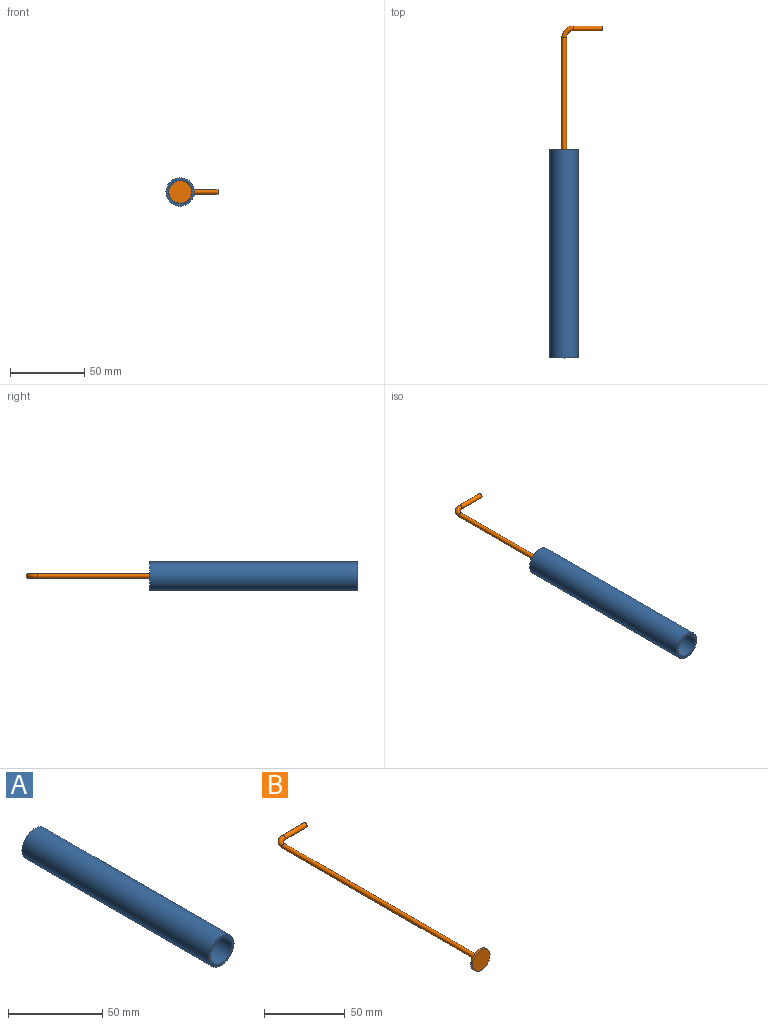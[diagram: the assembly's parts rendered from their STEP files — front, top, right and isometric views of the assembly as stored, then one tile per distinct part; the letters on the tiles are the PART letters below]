
ASSEMBLY  parts=2 mates=1
PART A: 6 faces, bbox 19.1x139.7x19.1 mm
  f0: cylinder r=7.94mm len=137.16mm, axis (0,1,0), area 6840.6mm2, adj f2,f5
  f1: cylinder r=9.53mm len=139.7mm, axis (0,1,0), area 8360.7mm2, adj f2,f3
  f2: plane 19.05x19.05mm, normal (0,-1,0), area 87.1mm2, adj f0,f1
  f3: plane 19.05x19.05mm, normal (0,1,0), area 277.1mm2, adj f1,f4
  f4: cylinder r=1.59mm len=3.18mm, axis (0,1,0), area 25.3mm2, adj f3,f5
  f5: plane 15.88x15.88mm, normal (0,-1,0), area 190mm2, adj f0,f4
PART B: 7 faces, bbox 33x181.6x15.2 mm
  f0: plane 3.18x3.18mm, normal (1,0,0), area 7.9mm2, adj f3
  f1: cylinder r=1.59mm len=171.45mm, axis (0,1,0), area 1710.1mm2, adj f2,f6
  f2: torus R=6.35mm, axis (0,0,-1), area 99.5mm2, adj f1,f3
  f3: cylinder r=1.59mm len=19.05mm, axis (1,0,0), area 190mm2, adj f0,f2
  f4: cylinder r=7.62mm len=15.24mm, axis (0,1,0), area 76mm2, adj f5,f6
  f5: plane 15.24x15.24mm, normal (0,-1,0), area 182.4mm2, adj f4
  f6: plane 15.24x15.24mm, normal (0,1,0), area 174.5mm2, adj f1,f4
PLACE A t=(-43.09,-131,-10.2)mm
PLACE B t=(-43.09,-227.21,-10.2)mm
MATE slider B.f1 <-> A.f4  axis (0,1,0) through (-43.09,-227.21,-10.2)mm
